# Revit family: Haworth_Cabana_IslandScreen
name_source: partatom
category: Furniture
revit_build: Autodesk Revit 2018 (Build: 20170223_1515(x64)
units: mm (PartAtom-declared; Revit-internal decimal feet)

## family parameters
Always vertical = Yes
Cut with Voids When Loaded = No
OmniClass Number = 23.40.70.14.64.21
OmniClass Title = Systems Furniture
Room Calculation Point = No
Shared = No
Work Plane-Based = No

## types (2) — shared parameters
Actual Depth = 1 65/256"
Actual Width = 54"
Assembly Code = E2020200
Manufacturer = Haworth
Model = Haworth Cabana Island
Revision Number = 1
Size = Verify Final Dim. w/ Haworth
URL = http://haworth.com
URL - Product = http://www.haworth.com
Warranty = http://www.haworth.com

## per-type parameters (varying)
| type | Actual Height | Description |
| High Screen | 44" | Haworth Cabana Island - High Screen |
| Low Screen | 34" | Haworth Cabana Island - Low Screen |

type visibility flags: 2 boolean params named "<type name>" — each type sets only its own to Yes (folded from table)

## geometry (parser evidence)
native form markers: Sweep x3
no freeform markers — native parametric forms only
